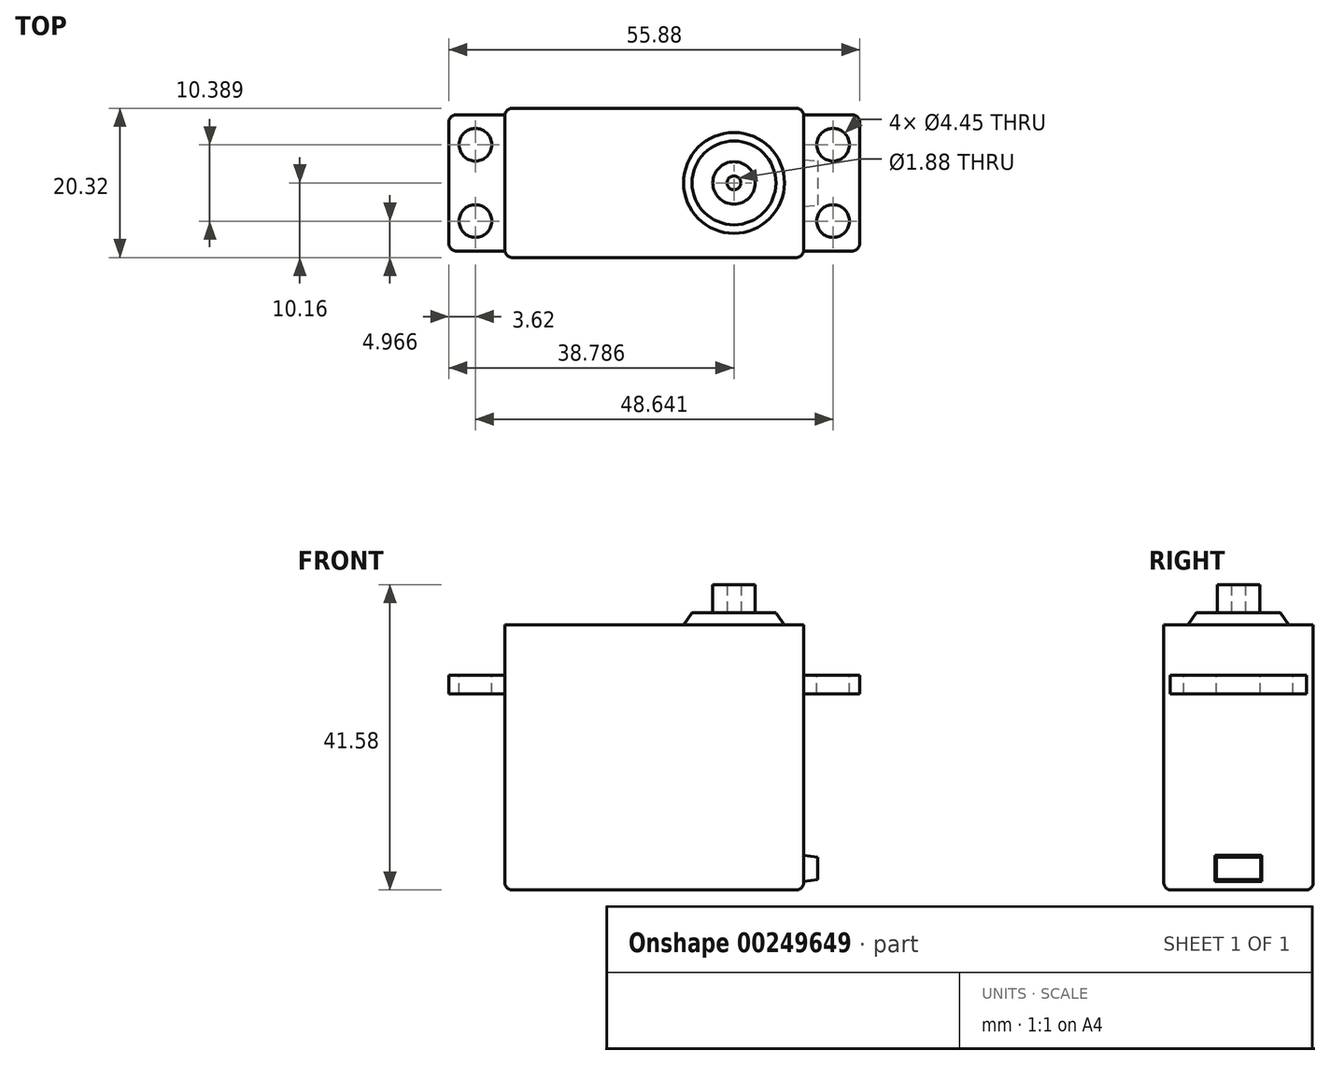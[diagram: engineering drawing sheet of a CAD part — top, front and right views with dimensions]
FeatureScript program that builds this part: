
annotation { "Feature Type Name" : "Feature", "Feature Type Description" : "" }
export const myFeature = defineFeature(function(context is Context, id is Id, definition is map)
    precondition{}
    {
        {
            var Q0;
            Q0=qCreatedBy(makeId("Top.planeOp"),FACE);
            var sketch = newSketch(context, id + "F0", { "sketchPlane" : qUnion([Q0])});
            skLineSegment(sketch, "E0.bottom", {"start": v(20.32, 10.16) * mm, "end": v(-20.32, 10.16) * mm});
            skLineSegment(sketch, "E0.top", {"start": v(20.32, -10.16) * mm, "end": v(-20.32, -10.16) * mm});
            skLineSegment(sketch, "E0.left", {"start": v(20.32, 10.16) * mm, "end": v(20.32, -10.16) * mm});
            skLineSegment(sketch, "E0.right", {"start": v(-20.32, 10.16) * mm, "end": v(-20.32, -10.16) * mm});
            skPoint(sketch, "E0.middle", {"position": v(0, 0) * mm});
            skSolve(sketch);
        }
        {
            var Q0;
            Q0=qSketchRegion(id+"F0",true);
            extrude(context, id + "F1", {"entities" : qUnion([Q0]), "depth" : 36.07 * mm});
        }
        {
            var Q0;
            Q0=makeQuery(id+"F1.opExtrude","SWEPT_FACE",FACE,{"disambiguationData":[OSD([sQuery(id+"F0.wireOp",EDGE,"E0.left")])]});
            var sketch = newSketch(context, id + "F2", { "sketchPlane" : qUnion([Q0])});
            skLineSegment(sketch, "E1.bottom", {"start": v(3.18, 4.75) * mm, "end": v(-3.17, 4.75) * mm});
            skLineSegment(sketch, "E1.top", {"start": v(3.18, 1.14) * mm, "end": v(-3.17, 1.14) * mm});
            skLineSegment(sketch, "E1.left", {"start": v(3.18, 4.75) * mm, "end": v(3.18, 1.14) * mm});
            skLineSegment(sketch, "E1.right", {"start": v(-3.17, 4.75) * mm, "end": v(-3.17, 1.14) * mm});
            skPoint(sketch, "E1.middle", {"position": v(0, 2.95) * mm});
            skSolve(sketch);
        }
        {
            var Q0;
            Q0=makeQuery(id+"F2.imprint","IMPRINT",FACE,{"disambiguationData":[TD([[makeQuery(id+"F2.imprint","IMPRINT",EDGE,{"derivedFrom":sQuery(id+"F2.wireOp",EDGE,"E1.bottom")}),-1.0]])]});
            cPlane(context, id + "F3", {"entities" : qUnion([Q0]), "cplaneType" : CPlaneType.OFFSET, "offset" : 1.9 * mm, "width" : 152.4 * mm, "height" : 152.4 * mm});
        }
        {
            var Q0;
            Q0=qCreatedBy(id+"F3.planeOp",FACE);
            var sketch = newSketch(context, id + "F4", { "sketchPlane" : qUnion([Q0])});
            skPoint(sketch, "E2.0", {"position": v(0, 2.95) * mm});
            skLineSegment(sketch, "E3.bottom", {"start": v(3, 4.48) * mm, "end": v(-3, 4.48) * mm});
            skLineSegment(sketch, "E3.top", {"start": v(3, 1.4) * mm, "end": v(-3, 1.4) * mm});
            skLineSegment(sketch, "E3.left", {"start": v(3, 4.48) * mm, "end": v(3, 1.4) * mm});
            skLineSegment(sketch, "E3.right", {"start": v(-3, 4.48) * mm, "end": v(-3, 1.4) * mm});
            skSolve(sketch);
        }
        {
            var Q1;
            Q1=makeQuery(id+"F2.imprint","IMPRINT",FACE,{"disambiguationData":[TD([[makeQuery(id+"F2.imprint","IMPRINT",EDGE,{"derivedFrom":sQuery(id+"F2.wireOp",EDGE,"E1.bottom")}),1.0]])]});
            var Q2;
            Q2=makeQuery(id+"F4.imprint","IMPRINT",FACE,{"disambiguationData":[TD([[makeQuery(id+"F4.imprint","IMPRINT",EDGE,{"derivedFrom":sQuery(id+"F4.wireOp",EDGE,"E3.bottom")}),1.0]])]});
            loft(context, id + "F5", {"operationType" : NewBodyOperationType.ADD, "sheetProfilesArray" : [{ "sheetProfileEntities" : qUnion([Q1]) }, { "sheetProfileEntities" : qUnion([Q2]) }]});
        }
        {
            var Q0;
            Q0=makeQuery(id+"F1.opExtrude","CAP_FACE",FACE,{"disambiguationData":[OSD([sQuery(id+"F0.wireOp",EDGE,"E0.bottom"),sQuery(id+"F0.wireOp",EDGE,"E0.top"),sQuery(id+"F0.wireOp",EDGE,"E0.left"),sQuery(id+"F0.wireOp",EDGE,"E0.right")])],"isStart":false});
            cPlane(context, id + "F6", {"entities" : qUnion([Q0]), "cplaneType" : CPlaneType.OFFSET, "offset" : 6.86 * mm, "oppositeDirection" : true, "width" : 152.4 * mm, "height" : 152.4 * mm});
        }
        {
            var Q0;
            Q0=qCreatedBy(id+"F6.planeOp",FACE);
            var sketch = newSketch(context, id + "F7", { "sketchPlane" : qUnion([Q0])});
            skLineSegment(sketch, "E4.bottom", {"start": v(-26.92, -9.27) * mm, "end": v(-20.32, -9.27) * mm});
            skLineSegment(sketch, "E4.top", {"start": v(-26.92, 9.27) * mm, "end": v(-20.32, 9.27) * mm});
            skLineSegment(sketch, "E4.left", {"start": v(-27.94, -8.25) * mm, "end": v(-27.94, 8.26) * mm});
            skLineSegment(sketch, "E4.right", {"start": v(-20.32, -9.27) * mm, "end": v(-20.32, 9.27) * mm});
            skPoint(sketch, "E4.middle", {"position": v(-24.13, 0) * mm});
            skLineSegment(sketch, "E5.0", {"start": v(-20.32, 10.16) * mm, "end": v(-20.32, -10.16) * mm});
            skPoint(sketch, "E6.visualSharp", {"position": v(-27.94, -9.27) * mm});
            skArc(sketch, "E6.filletArc", {"start": v(-27.94, -8.25) * mm, "mid": v(-27.64, -8.97) * mm, "end": v(-26.92, -9.27) * mm});
            skPoint(sketch, "E7.visualSharp", {"position": v(-27.94, 9.27) * mm});
            skArc(sketch, "E7.filletArc", {"start": v(-26.92, 9.27) * mm, "mid": v(-27.64, 8.97) * mm, "end": v(-27.94, 8.26) * mm});
            skCircle(sketch, "E8", {"center": v(-24.32, -5.2) * mm, "radius": 2.22 * mm});
            skCircle(sketch, "E9.MirrorC", {"center": v(-24.32, 5.2) * mm, "radius": 2.22 * mm});
            skLineSegment(sketch, "E10.MirrorCS", {"start": v(26.92, 9.27) * mm, "end": v(20.32, 9.27) * mm});
            skArc(sketch, "E11.MirrorCS", {"start": v(26.92, 9.27) * mm, "mid": v(27.64, 8.97) * mm, "end": v(27.94, 8.26) * mm});
            skLineSegment(sketch, "E12.MirrorCS", {"start": v(27.94, -8.25) * mm, "end": v(27.94, 8.26) * mm});
            skArc(sketch, "E13.MirrorCS", {"start": v(27.94, -8.25) * mm, "mid": v(27.64, -8.97) * mm, "end": v(26.92, -9.27) * mm});
            skLineSegment(sketch, "E14.MirrorCS", {"start": v(26.92, -9.27) * mm, "end": v(20.32, -9.27) * mm});
            skCircle(sketch, "E15.MirrorC", {"center": v(24.32, -5.2) * mm, "radius": 2.22 * mm});
            skCircle(sketch, "E16.MirrorC", {"center": v(24.32, 5.2) * mm, "radius": 2.22 * mm});
            skLineSegment(sketch, "E17.MirrorCS", {"start": v(20.32, 10.16) * mm, "end": v(20.32, -10.16) * mm});
            skSolve(sketch);
        }
        {
            var Q0;
            Q0=qSketchRegion(id+"F7",true);
            extrude(context, id + "F8", {"entities" : qUnion([Q0]), "operationType" : NewBodyOperationType.ADD, "oppositeDirection" : true, "depth" : 2.54 * mm});
        }
        {
            var Q0;
            Q0=makeQuery(id+"F1.opExtrude","CAP_FACE",FACE,{"disambiguationData":[OSD([sQuery(id+"F0.wireOp",EDGE,"E0.bottom"),sQuery(id+"F0.wireOp",EDGE,"E0.top"),sQuery(id+"F0.wireOp",EDGE,"E0.left"),sQuery(id+"F0.wireOp",EDGE,"E0.right")])],"isStart":false});
            var sketch = newSketch(context, id + "F9", { "sketchPlane" : qUnion([Q0])});
            skCircle(sketch, "E18", {"center": v(10.85, 0) * mm, "radius": 6.86 * mm});
            skSolve(sketch);
        }
        {
            var Q0;
            Q0=makeQuery(id+"F1.opExtrude","CAP_FACE",FACE,{"disambiguationData":[OSD([sQuery(id+"F0.wireOp",EDGE,"E0.bottom"),sQuery(id+"F0.wireOp",EDGE,"E0.top"),sQuery(id+"F0.wireOp",EDGE,"E0.left"),sQuery(id+"F0.wireOp",EDGE,"E0.right")])],"isStart":false});
            cPlane(context, id + "F10", {"entities" : qUnion([Q0]), "cplaneType" : CPlaneType.OFFSET, "offset" : 1.65 * mm, "width" : 152.4 * mm, "height" : 152.4 * mm});
        }
        {
            var Q0;
            Q0=qCreatedBy(id+"F10.planeOp",FACE);
            var sketch = newSketch(context, id + "F11", { "sketchPlane" : qUnion([Q0])});
            skPoint(sketch, "E19.0", {"position": v(10.85, 0) * mm});
            skCircle(sketch, "E20", {"center": v(10.85, 0) * mm, "radius": 5.7 * mm});
            skSolve(sketch);
        }
        {
            var Q1;
            Q1=makeQuery(id+"F9.imprint","IMPRINT",FACE,{"disambiguationData":[TD([[makeQuery(id+"F9.imprint","IMPRINT",EDGE,{"derivedFrom":sQuery(id+"F9.wireOp",EDGE,"E18")}),1.0]])]});
            var Q2;
            Q2=makeQuery(id+"F11.imprint","IMPRINT",FACE,{"disambiguationData":[TD([[makeQuery(id+"F11.imprint","IMPRINT",EDGE,{"derivedFrom":sQuery(id+"F11.wireOp",EDGE,"E20")}),1.0]])]});
            loft(context, id + "F12", {"operationType" : NewBodyOperationType.ADD, "sheetProfilesArray" : [{ "sheetProfileEntities" : qUnion([Q1]) }, { "sheetProfileEntities" : qUnion([Q2]) }]});
        }
        {
            var Q0;
            Q0=makeQuery(id+"F1.opExtrude","SWEPT_EDGE",EDGE,{"disambiguationData":[OSD([sQuery(id+"F0.wireOp",EDGE,"E0.top"),sQuery(id+"F0.wireOp",EDGE,"E0.left")])]});
            var Q1;
            Q1=makeQuery(id+"F1.opExtrude","SWEPT_EDGE",EDGE,{"disambiguationData":[OSD([sQuery(id+"F0.wireOp",EDGE,"E0.bottom"),sQuery(id+"F0.wireOp",EDGE,"E0.left")])]});
            var Q2;
            Q2=makeQuery(id+"F1.opExtrude","SWEPT_EDGE",EDGE,{"disambiguationData":[OSD([sQuery(id+"F0.wireOp",EDGE,"E0.bottom"),sQuery(id+"F0.wireOp",EDGE,"E0.right")])]});
            var Q3;
            Q3=makeQuery(id+"F1.opExtrude","SWEPT_EDGE",EDGE,{"disambiguationData":[OSD([sQuery(id+"F0.wireOp",EDGE,"E0.top"),sQuery(id+"F0.wireOp",EDGE,"E0.right")])]});
            var Q4;
            Q4=makeQuery(id+"F1.opExtrude","CAP_EDGE",EDGE,{"disambiguationData":[OSD([sQuery(id+"F0.wireOp",EDGE,"E0.top")])],"isStart":true});
            var Q5;
            Q5=makeQuery(id+"F1.opExtrude","CAP_EDGE",EDGE,{"disambiguationData":[OSD([sQuery(id+"F0.wireOp",EDGE,"E0.left")])],"isStart":true});
            var Q6;
            Q6=makeQuery(id+"F1.opExtrude","CAP_EDGE",EDGE,{"disambiguationData":[OSD([sQuery(id+"F0.wireOp",EDGE,"E0.bottom")])],"isStart":true});
            var Q7;
            Q7=makeQuery(id+"F1.opExtrude","CAP_EDGE",EDGE,{"disambiguationData":[OSD([sQuery(id+"F0.wireOp",EDGE,"E0.right")])],"isStart":true});
            fillet(context, id + "F13", {"entities" : qUnion([Q0, Q1, Q2, Q3, Q4, Q5, Q6, Q7]), "radius" : 1.02 * mm, "tangentPropagation" : true, "allowEdgeOverflow" : false});
        }
        {
            var Q0;
            Q0=makeQuery(id+"F12.opLoft","CAP_FACE",FACE,{"disambiguationData":[OSD([makeQuery(id+"F11.imprint","IMPRINT",FACE,{"disambiguationData":[TD([[makeQuery(id+"F11.imprint","IMPRINT",EDGE,{"derivedFrom":sQuery(id+"F11.wireOp",EDGE,"E20")}),1.0]])]})])],"isStart":true});
            var sketch = newSketch(context, id + "F14", { "sketchPlane" : qUnion([Q0])});
            skPoint(sketch, "E21.0", {"position": v(10.85, 0) * mm});
            skCircle(sketch, "E22", {"center": v(10.85, 0) * mm, "radius": 2.88 * mm});
            skCircle(sketch, "E23", {"center": v(10.85, 0) * mm, "radius": 0.94 * mm});
            skSolve(sketch);
        }
        {
            var Q0;
            Q0=qSketchRegion(id+"F14",true);
            extrude(context, id + "F15", {"entities" : qUnion([Q0]), "depth" : 3.86 * mm});
        }
    });
